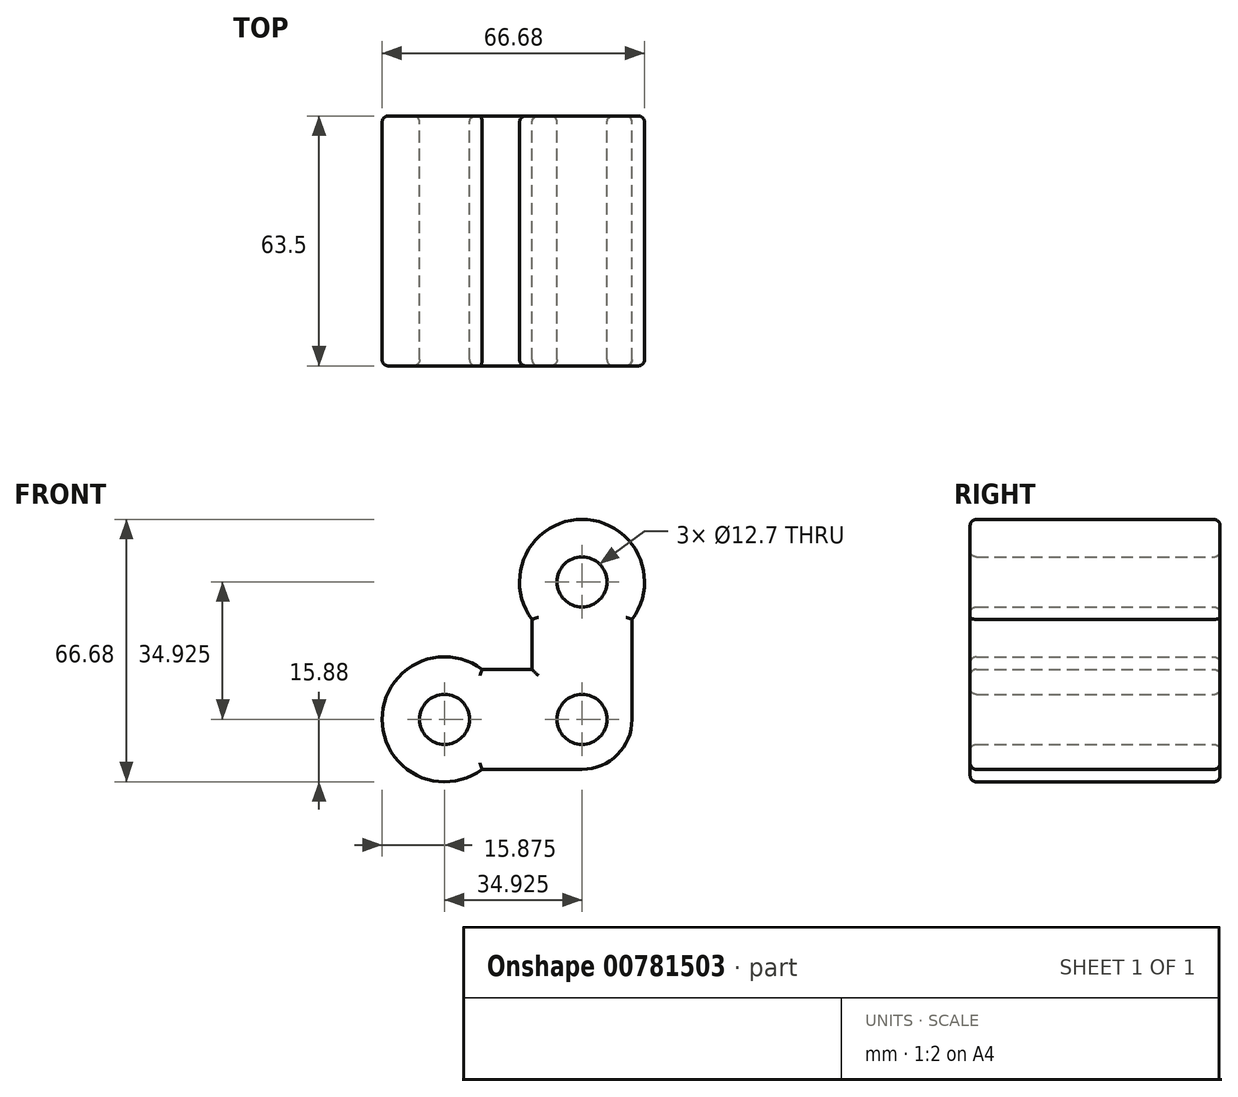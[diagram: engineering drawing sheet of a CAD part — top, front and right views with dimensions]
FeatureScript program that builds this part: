
annotation { "Feature Type Name" : "Feature", "Feature Type Description" : "" }
export const myFeature = defineFeature(function(context is Context, id is Id, definition is map)
    precondition{}
    {
        {
            var Q0;
            Q0=qCreatedBy(makeId("Front.planeOp"),FACE);
            var sketch = newSketch(context, id + "F0", { "sketchPlane" : qUnion([Q0])});
            skPoint(sketch, "E0.middle", {"position": v(0, 0) * mm});
            skArc(sketch, "E1", {"start": v(-25.4, 12.7) * mm, "mid": v(-50.8, 0) * mm, "end": v(-25.4, -12.7) * mm});
            skCircle(sketch, "E2", {"center": v(-34.93, 0) * mm, "radius": 6.35 * mm});
            skCircle(sketch, "E3", {"center": v(0, 0) * mm, "radius": 6.35 * mm});
            skArc(sketch, "E4", {"start": v(12.7, 25.4) * mm, "mid": v(0, 50.8) * mm, "end": v(-12.7, 25.4) * mm});
            skCircle(sketch, "E5", {"center": v(0, 34.93) * mm, "radius": 6.35 * mm});
            skLineSegment(sketch, "E6", {"start": v(-25.4, 12.7) * mm, "end": v(-12.7, 12.7) * mm});
            skLineSegment(sketch, "E7", {"start": v(-12.7, 12.7) * mm, "end": v(-12.7, 25.4) * mm});
            skLineSegment(sketch, "E8", {"start": v(0, 0) * mm, "end": v(0, -12.7) * mm, "construction": true});
            skLineSegment(sketch, "E9", {"start": v(0, 0) * mm, "end": v(12.7, 0) * mm, "construction": true});
            skArc(sketch, "E10", {"start": v(0, -12.7) * mm, "mid": v(8.98, -8.98) * mm, "end": v(12.7, 0) * mm});
            skLineSegment(sketch, "E11", {"start": v(-25.4, -12.7) * mm, "end": v(0, -12.7) * mm});
            skLineSegment(sketch, "E12", {"start": v(12.7, 25.4) * mm, "end": v(12.7, 0) * mm});
            skLineSegment(sketch, "E13", {"start": v(0, 34.93) * mm, "end": v(0, 0) * mm, "construction": true});
            skLineSegment(sketch, "E14", {"start": v(-34.93, 0) * mm, "end": v(0, 0) * mm, "construction": true});
            skSolve(sketch);
        }
        {
            var Q0;
            Q0 = qSketchRegion(id + "F0", true);
            extrude(context, id + "F1", {"entities" : qUnion([Q0]), "depth" : 63.5 * mm, "offsetDistance" : 25.4 * mm});
        }
        {
            var Q0;
            Q0=makeQuery(id+"F1.opExtrude","CAP_FACE",FACE,{"disambiguationData":[OSD([sQuery(id+"F0.wireOp",EDGE,"E0.bottom"),sQuery(id+"F0.wireOp",EDGE,"E0.top"),sQuery(id+"F0.wireOp",EDGE,"E1"),sQuery(id+"F0.wireOp",EDGE,"HU005968-EPoc-hUcn-3xDy-Z5oug8kM1b02"),sQuery(id+"F0.wireOp",EDGE,"E2"),sQuery(id+"F0.wireOp",EDGE,"AkObAe3M-WMde-RekC-m5AX-zwr52MaSNqkG")])],"isStart":false});
            var Q1;
            Q1=makeQuery(id+"F1.opExtrude","CAP_FACE",FACE,{"disambiguationData":[OSD([sQuery(id+"F0.wireOp",EDGE,"E0.bottom"),sQuery(id+"F0.wireOp",EDGE,"E0.top"),sQuery(id+"F0.wireOp",EDGE,"E1"),sQuery(id+"F0.wireOp",EDGE,"HU005968-EPoc-hUcn-3xDy-Z5oug8kM1b02"),sQuery(id+"F0.wireOp",EDGE,"E2"),sQuery(id+"F0.wireOp",EDGE,"AkObAe3M-WMde-RekC-m5AX-zwr52MaSNqkG")])],"isStart":true});
            var Q2;
            Q2=makeQuery(id+"F1.opExtrude","SWEPT_EDGE",EDGE,{"disambiguationData":[OSD([sQuery(id+"F0.wireOp",EDGE,"0tC4kBdZ-CyGd-Yq8B-8fgO-Dqxgf3bIaCrt"),sQuery(id+"F0.wireOp",EDGE,"weq4sHNp-Fmh5-bx1M-teIE-JfKgd8E8dN0F")])]});
            fillet(context, id + "F2", {"entities" : qUnion([Q0, Q1, Q2]), "radius" : 1.59 * mm, "tangentPropagation" : true, "allowEdgeOverflow" : false});
        }
    });
